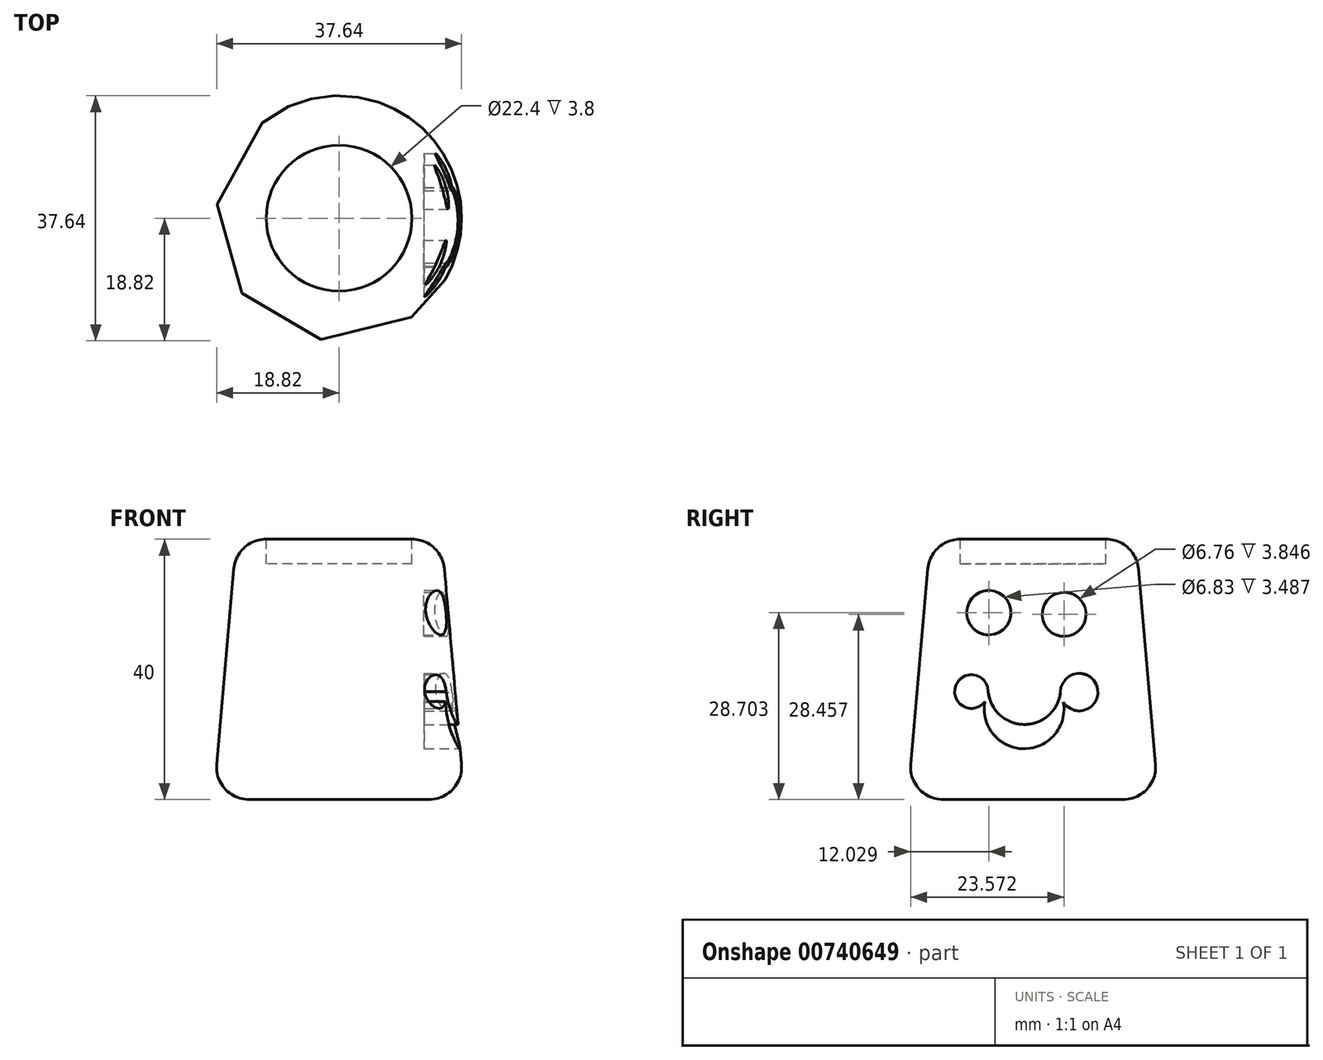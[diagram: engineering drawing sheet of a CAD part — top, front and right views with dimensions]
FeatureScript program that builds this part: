
annotation { "Feature Type Name" : "Feature", "Feature Type Description" : "" }
export const myFeature = defineFeature(function(context is Context, id is Id, definition is map)
    precondition{}
    {
        {
            var Q0;
            Q0=qCreatedBy(makeId("Top.planeOp"),FACE);
            var sketch = newSketch(context, id + "F0", { "sketchPlane" : qUnion([Q0])});
            skCircle(sketch, "E0", {"center": v(0, 0) * mm, "radius": 19.28 * mm});
            skSolve(sketch);
        }
        {
            var Q0;
            Q0=makeQuery(id+"F0.imprint","IMPRINT",FACE,{"disambiguationData":[TD([[makeQuery(id+"F0.imprint","IMPRINT",EDGE,{"derivedFrom":sQuery(id+"F0.wireOp",EDGE,"E0")}),1.0]])]});
            extrude(context, id + "F1", {"entities" : qUnion([Q0]), "depth" : 40 * mm, "offsetDistance" : 25 * mm, "hasDraft" : true, "draftAngle" : 5 * degree, "draftPullDirection" : true});
        }
        {
            var Q0;
            Q0=makeQuery(id+"F1.opExtrude","CAP_EDGE",EDGE,{"disambiguationData":[OSD([sQuery(id+"F0.wireOp",EDGE,"E0")])],"isStart":false});
            var Q1;
            Q1=makeQuery(id+"F1.opExtrude","CAP_EDGE",EDGE,{"disambiguationData":[OSD([sQuery(id+"F0.wireOp",EDGE,"E0")])],"isStart":true});
            fillet(context, id + "F2", {"entities" : qUnion([Q0, Q1]), "radius" : 5 * mm, "tangentPropagation" : true, "allowEdgeOverflow" : false});
        }
        {
            var Q0;
            Q0=qCreatedBy(makeId("Right.planeOp"),FACE);
            cPlane(context, id + "F3", {"entities" : qUnion([Q0]), "cplaneType" : CPlaneType.OFFSET, "offset" : 25 * mm, "width" : 150 * mm, "height" : 150 * mm});
        }
        {
            var Q0;
            Q0=qCreatedBy(id+"F3.planeOp",FACE);
            var sketch = newSketch(context, id + "F4", { "sketchPlane" : qUnion([Q0])});
            skArc(sketch, "E1", {"start": v(4.66, 14.94) * mm, "mid": v(9.84, 17.34) * mm, "end": v(4.2, 16.44) * mm});
            skArc(sketch, "E2", {"start": v(-6.9, 16.57) * mm, "mid": v(-11.93, 17.39) * mm, "end": v(-7.39, 15.06) * mm});
            skPoint(sketch, "E2.centerSnap0", {"position": v(-9.48, 22.7) * mm});
            skCircle(sketch, "E3", {"center": v(-6.8, 28.7) * mm, "radius": 3.41 * mm});
            skCircle(sketch, "E4", {"center": v(4.75, 28.46) * mm, "radius": 3.38 * mm});
            skArc(sketch, "E5", {"start": v(-6.9, 16.57) * mm, "mid": v(-1.4, 11.53) * mm, "end": v(4.2, 16.44) * mm});
            skArc(sketch, "E6", {"start": v(-7.39, 15.06) * mm, "mid": v(-1.44, 7.8) * mm, "end": v(4.66, 14.94) * mm});
            skSolve(sketch);
        }
        {
            var Q0;
            Q0=makeQuery(id+"F4.imprint","IMPRINT",FACE,{"disambiguationData":[TD([[makeQuery(id+"F4.imprint","IMPRINT",EDGE,{"derivedFrom":sQuery(id+"F4.wireOp",EDGE,"E3")}),1.0]])]});
            var Q1;
            Q1=makeQuery(id+"F4.imprint","IMPRINT",FACE,{"disambiguationData":[TD([[makeQuery(id+"F4.imprint","IMPRINT",EDGE,{"derivedFrom":sQuery(id+"F4.wireOp",EDGE,"E4")}),1.0]])]});
            extrude(context, id + "F5", {"entities" : qUnion([Q0, Q1]), "operationType" : NewBodyOperationType.REMOVE, "oppositeDirection" : true, "depth" : 12 * mm, "offsetDistance" : 25 * mm});
        }
        {
            var Q0;
            Q0=makeQuery(id+"F4.imprint","IMPRINT",FACE,{"disambiguationData":[TD([[makeQuery(id+"F4.imprint","IMPRINT",EDGE,{"derivedFrom":sQuery(id+"F4.wireOp",EDGE,"E1")}),1.0]])]});
            extrude(context, id + "F6", {"entities" : qUnion([Q0]), "operationType" : NewBodyOperationType.REMOVE, "oppositeDirection" : true, "depth" : 11.9 * mm, "offsetDistance" : 25 * mm});
        }
        {
            var Q0;
            Q0=makeQuery(id+"F1.opExtrude","CAP_FACE",FACE,{"disambiguationData":[OSD([sQuery(id+"F0.wireOp",EDGE,"E0")])],"isStart":false});
            var sketch = newSketch(context, id + "F7", { "sketchPlane" : qUnion([Q0])});
            skSolve(sketch);
        }
        {
            var Q0;
            Q0 = qSketchRegion(id + "F7", true);
            var Q1;
            {var subQ0=sQuery(id+"F0.wireOp",EDGE,"E0");Q1=makeQuery(id+"F7.imprint","IMPRINT",FACE,{"disambiguationData":[TD([[makeQuery(id+"F7.imprint","IMPRINT",EDGE,{"derivedFrom":makeQuery(id+"F2.opFillet","BLEND_EDGE",EDGE,{"blendedFrom":[makeQuery(id+"F1.opExtrude","CAP_EDGE",EDGE,{"disambiguationData":[OSD([subQ0])],"isStart":false}),makeQuery(id+"F1.opExtrude","CAP_FACE",FACE,{"disambiguationData":[OSD([subQ0])],"isStart":false})],"blendedInto":[makeQuery(id+"F1.opExtrude","CAP_FACE",FACE,{"disambiguationData":[OSD([subQ0])],"isStart":false})]})}),1.0]])]});}
            extrude(context, id + "F8", {"entities" : qUnion([Q0, Q1]), "operationType" : NewBodyOperationType.REMOVE, "oppositeDirection" : true, "depth" : 3.8 * mm, "offsetDistance" : 25 * mm});
        }
    });
